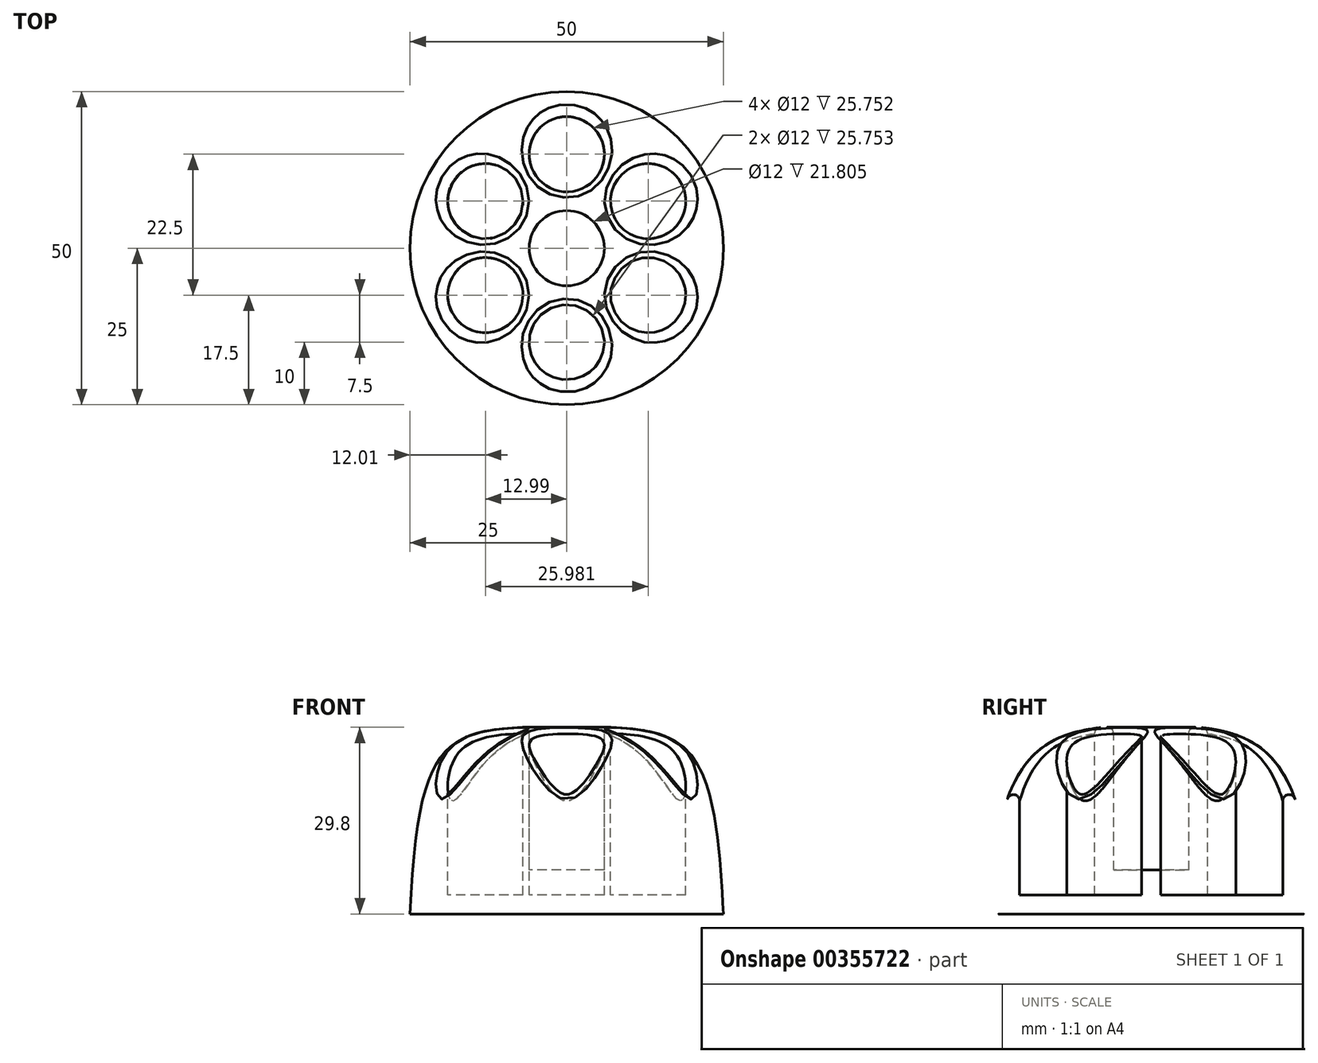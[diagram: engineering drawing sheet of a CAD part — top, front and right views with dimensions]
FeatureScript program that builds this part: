
annotation { "Feature Type Name" : "Feature", "Feature Type Description" : "" }
export const myFeature = defineFeature(function(context is Context, id is Id, definition is map)
    precondition{}
    {
        {
            var Q0;
            Q0=qCreatedBy(makeId("Top.planeOp"),FACE);
            var sketch = newSketch(context, id + "F0", { "sketchPlane" : qUnion([Q0])});
            skCircle(sketch, "E0", {"center": v(0, 0) * mm, "radius": 15 * mm});
            skCircle(sketch, "E1", {"center": v(0, 15) * mm, "radius": 6 * mm});
            skCircle(sketch, "E2.1.0", {"center": v(-13, 7.5) * mm, "radius": 6 * mm});
            skCircle(sketch, "E2.2.0", {"center": v(-13, -7.5) * mm, "radius": 6 * mm});
            skCircle(sketch, "E2.3.0", {"center": v(0, -15) * mm, "radius": 6 * mm});
            skCircle(sketch, "E2.4.0", {"center": v(13, -7.5) * mm, "radius": 6 * mm});
            skCircle(sketch, "E2.5.0", {"center": v(13, 7.5) * mm, "radius": 6 * mm});
            skCircle(sketch, "E3", {"center": v(0, 0) * mm, "radius": 6 * mm});
            skCircle(sketch, "E4", {"center": v(0, 0) * mm, "radius": 25 * mm});
            skLineSegment(sketch, "E5", {"start": v(0, 0) * mm, "end": v(25, 0) * mm});
            skSolve(sketch);
        }
        {
            var Q0;
            Q0=qCreatedBy(makeId("Front.planeOp"),FACE);
            var sketch = newSketch(context, id + "F1", { "sketchPlane" : qUnion([Q0])});
            skLineSegment(sketch, "E6.0", {"start": v(0, 0) * mm, "end": v(25, 0) * mm});
            skLineSegment(sketch, "E7", {"start": v(0, 0) * mm, "end": v(0, 30) * mm});
            skFitSpline(sketch, "E8", {"points": [v(0, 30) * mm, v(25, 0) * mm], "startDerivative": vector(57.03, -1.32) * mm, "endDerivative": vector(4.21, -91) * mm});
            skSolve(sketch);
        }
        {
            var Q0;
            Q0=makeQuery(id+"F1.imprint","IMPRINT",FACE,{"disambiguationData":[TD([[makeQuery(id+"F1.imprint","IMPRINT",EDGE,{"derivedFrom":sQuery(id+"F1.wireOp",EDGE,"E6.0")}),1.0]])]});
            var Q1;
            Q1=sQuery(id+"F1.wireOp",EDGE,"E7");
            revolve(context, id + "F2", {"entities" : qUnion([Q0]), "axis" : qUnion([Q1]), "revolveType" : RevolveType.FULL});
        }
        {
            var Q0;
            Q0=makeQuery(id+"F0.imprint","IMPRINT",FACE,{"disambiguationData":[TD([[makeQuery(id+"F0.imprint","IMPRINT",EDGE,{"derivedFrom":sQuery(id+"F0.wireOp",EDGE,"E4")}),1.0]])]});
            cPlane(context, id + "F3", {"entities" : qUnion([Q0]), "cplaneType" : CPlaneType.OFFSET, "offset" : 30 * mm, "width" : 150 * mm, "height" : 150 * mm});
        }
        {
            var Q0;
            Q0=qCreatedBy(id+"F3.planeOp",FACE);
            var sketch = newSketch(context, id + "F4", { "sketchPlane" : qUnion([Q0])});
            skCircle(sketch, "E9.0", {"center": v(0, 15) * mm, "radius": 6 * mm});
            skCircle(sketch, "E9.1", {"center": v(13, 7.5) * mm, "radius": 6 * mm});
            skCircle(sketch, "E9.2", {"center": v(0, 0) * mm, "radius": 6 * mm});
            skCircle(sketch, "E9.3", {"center": v(13, -7.5) * mm, "radius": 6 * mm});
            skCircle(sketch, "E9.4", {"center": v(0, -15) * mm, "radius": 6 * mm});
            skCircle(sketch, "E9.5", {"center": v(-13, -7.5) * mm, "radius": 6 * mm});
            skCircle(sketch, "E9.6", {"center": v(-13, 7.5) * mm, "radius": 6 * mm});
            skSolve(sketch);
        }
        {
            var Q0;
            Q0=makeQuery(id+"F4.imprint","IMPRINT",FACE,{"disambiguationData":[TD([[makeQuery(id+"F4.imprint","IMPRINT",EDGE,{"derivedFrom":sQuery(id+"F4.wireOp",EDGE,"E9.1")}),1.0]])]});
            var Q1;
            Q1=makeQuery(id+"F4.imprint","IMPRINT",FACE,{"disambiguationData":[TD([[makeQuery(id+"F4.imprint","IMPRINT",EDGE,{"derivedFrom":sQuery(id+"F4.wireOp",EDGE,"E9.0")}),1.0]])]});
            var Q2;
            Q2=makeQuery(id+"F4.imprint","IMPRINT",FACE,{"disambiguationData":[TD([[makeQuery(id+"F4.imprint","IMPRINT",EDGE,{"derivedFrom":sQuery(id+"F4.wireOp",EDGE,"E9.6")}),1.0]])]});
            var Q3;
            Q3=makeQuery(id+"F4.imprint","IMPRINT",FACE,{"disambiguationData":[TD([[makeQuery(id+"F4.imprint","IMPRINT",EDGE,{"derivedFrom":sQuery(id+"F4.wireOp",EDGE,"E9.5")}),1.0]])]});
            var Q4;
            Q4=makeQuery(id+"F4.imprint","IMPRINT",FACE,{"disambiguationData":[TD([[makeQuery(id+"F4.imprint","IMPRINT",EDGE,{"derivedFrom":sQuery(id+"F4.wireOp",EDGE,"E9.3")}),1.0]])]});
            var Q5;
            Q5=makeQuery(id+"F4.imprint","IMPRINT",FACE,{"disambiguationData":[TD([[makeQuery(id+"F4.imprint","IMPRINT",EDGE,{"derivedFrom":sQuery(id+"F4.wireOp",EDGE,"E9.4")}),1.0]])]});
            extrude(context, id + "F5", {"entities" : qUnion([Q0, Q1, Q2, Q3, Q4, Q5]), "operationType" : NewBodyOperationType.REMOVE, "oppositeDirection" : true, "depth" : 27 * mm});
        }
        {
            var Q0;
            Q0=makeQuery(id+"F4.imprint","IMPRINT",FACE,{"disambiguationData":[TD([[makeQuery(id+"F4.imprint","IMPRINT",EDGE,{"derivedFrom":sQuery(id+"F4.wireOp",EDGE,"E9.2")}),1.0]])]});
            extrude(context, id + "F6", {"entities" : qUnion([Q0]), "operationType" : NewBodyOperationType.REMOVE, "oppositeDirection" : true, "depth" : 23 * mm});
        }
        {
            var Q0;
            Q0=makeQuery(id+"F5.boolean.opBoolean","INTERSECT",EDGE,{"derivedFrom":[makeQuery(id+"F2.opRevolve","SWEPT_FACE",FACE,{"disambiguationData":[OSD([sQuery(id+"F1.wireOp",EDGE,"E8")])]}),makeQuery(id+"F5.opExtrude","SWEPT_FACE",FACE,{"disambiguationData":[OSD([sQuery(id+"F4.wireOp",EDGE,"E9.0")])]})]});
            var Q1;
            Q1=makeQuery(id+"F5.boolean.opBoolean","INTERSECT",EDGE,{"derivedFrom":[makeQuery(id+"F2.opRevolve","SWEPT_FACE",FACE,{"disambiguationData":[OSD([sQuery(id+"F1.wireOp",EDGE,"E8")])]}),makeQuery(id+"F5.opExtrude","SWEPT_FACE",FACE,{"disambiguationData":[OSD([sQuery(id+"F4.wireOp",EDGE,"E9.6")])]})]});
            var Q2;
            Q2=makeQuery(id+"F6.boolean.opBoolean","INTERSECT",EDGE,{"derivedFrom":[makeQuery(id+"F2.opRevolve","SWEPT_FACE",FACE,{"disambiguationData":[OSD([sQuery(id+"F1.wireOp",EDGE,"E8")])]}),makeQuery(id+"F6.opExtrude","SWEPT_FACE",FACE,{"disambiguationData":[OSD([sQuery(id+"F4.wireOp",EDGE,"E9.2")])]})]});
            var Q3;
            Q3=makeQuery(id+"F5.boolean.opBoolean","INTERSECT",EDGE,{"derivedFrom":[makeQuery(id+"F2.opRevolve","SWEPT_FACE",FACE,{"disambiguationData":[OSD([sQuery(id+"F1.wireOp",EDGE,"E8")])]}),makeQuery(id+"F5.opExtrude","SWEPT_FACE",FACE,{"disambiguationData":[OSD([sQuery(id+"F4.wireOp",EDGE,"E9.3")])]})]});
            var Q4;
            Q4=makeQuery(id+"F5.boolean.opBoolean","INTERSECT",EDGE,{"derivedFrom":[makeQuery(id+"F2.opRevolve","SWEPT_FACE",FACE,{"disambiguationData":[OSD([sQuery(id+"F1.wireOp",EDGE,"E8")])]}),makeQuery(id+"F5.opExtrude","SWEPT_FACE",FACE,{"disambiguationData":[OSD([sQuery(id+"F4.wireOp",EDGE,"E9.4")])]})]});
            var Q5;
            Q5=makeQuery(id+"F5.boolean.opBoolean","INTERSECT",EDGE,{"derivedFrom":[makeQuery(id+"F2.opRevolve","SWEPT_FACE",FACE,{"disambiguationData":[OSD([sQuery(id+"F1.wireOp",EDGE,"E8")])]}),makeQuery(id+"F5.opExtrude","SWEPT_FACE",FACE,{"disambiguationData":[OSD([sQuery(id+"F4.wireOp",EDGE,"E9.5")])]})]});
            var Q6;
            Q6=makeQuery(id+"F5.boolean.opBoolean","INTERSECT",EDGE,{"derivedFrom":[makeQuery(id+"F2.opRevolve","SWEPT_FACE",FACE,{"disambiguationData":[OSD([sQuery(id+"F1.wireOp",EDGE,"E8")])]}),makeQuery(id+"F5.opExtrude","SWEPT_FACE",FACE,{"disambiguationData":[OSD([sQuery(id+"F4.wireOp",EDGE,"E9.1")])]})]});
            fillet(context, id + "F7", {"entities" : qUnion([Q0, Q1, Q2, Q3, Q4, Q5, Q6]), "radius" : 1 * mm, "tangentPropagation" : true, "allowEdgeOverflow" : false});
        }
    });
